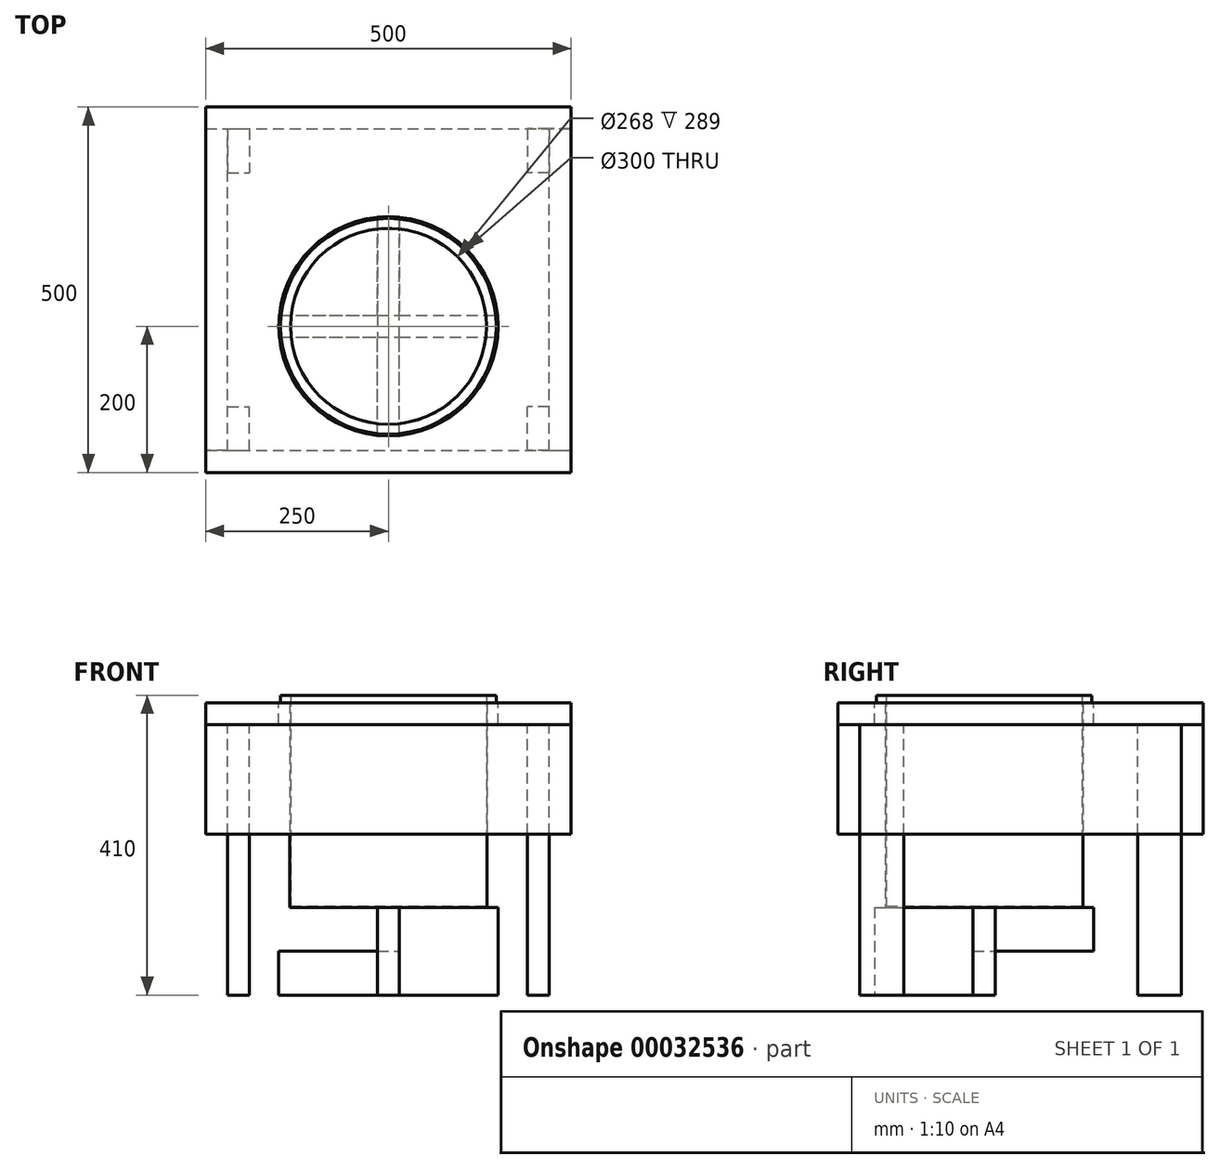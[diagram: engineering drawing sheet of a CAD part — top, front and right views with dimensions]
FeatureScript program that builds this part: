
annotation { "Feature Type Name" : "Feature", "Feature Type Description" : "" }
export const myFeature = defineFeature(function(context is Context, id is Id, definition is map)
    precondition{}
    {
        {
            var Q0;
            Q0=qCreatedBy(makeId("Top.planeOp"),FACE);
            var sketch = newSketch(context, id + "F0", { "sketchPlane" : qUnion([Q0])});
            skLineSegment(sketch, "E0.bottom", {"start": v(0, 0) * mm, "end": v(500, 0) * mm});
            skLineSegment(sketch, "E0.top", {"start": v(0, 500) * mm, "end": v(500, 500) * mm});
            skLineSegment(sketch, "E0.left", {"start": v(0, 0) * mm, "end": v(0, 500) * mm});
            skLineSegment(sketch, "E0.right", {"start": v(500, 0) * mm, "end": v(500, 500) * mm});
            skSolve(sketch);
        }
        {
            var Q0;
            Q0=makeQuery(id+"F0.imprint","IMPRINT",FACE,{"disambiguationData":[TD([[makeQuery(id+"F0.imprint","IMPRINT",EDGE,{"derivedFrom":sQuery(id+"F0.wireOp",EDGE,"E0.bottom")}),1.0]])]});
            extrude(context, id + "F1", {"entities" : qUnion([Q0]), "depth" : 30 * mm});
        }
        {
            var Q0;
            Q0=makeQuery(id+"F1.opExtrude","CAP_FACE",FACE,{"disambiguationData":[OSD([sQuery(id+"F0.wireOp",EDGE,"E0.bottom"),sQuery(id+"F0.wireOp",EDGE,"E0.top"),sQuery(id+"F0.wireOp",EDGE,"E0.left"),sQuery(id+"F0.wireOp",EDGE,"E0.right")])],"isStart":true});
            var sketch = newSketch(context, id + "F2", { "sketchPlane" : qUnion([Q0])});
            skLineSegment(sketch, "E1.bottom", {"start": v(30, -30) * mm, "end": v(60, -30) * mm});
            skLineSegment(sketch, "E1.top", {"start": v(30, -90) * mm, "end": v(60, -90) * mm});
            skLineSegment(sketch, "E1.left", {"start": v(30, -30) * mm, "end": v(30, -90) * mm});
            skLineSegment(sketch, "E1.right", {"start": v(60, -30) * mm, "end": v(60, -90) * mm});
            skLineSegment(sketch, "E2", {"start": v(30, -30) * mm, "end": v(30, 0) * mm, "construction": true});
            skLineSegment(sketch, "E3", {"start": v(30, -30) * mm, "end": v(0, -30) * mm, "construction": true});
            skLineSegment(sketch, "E4", {"start": v(250, 0) * mm, "end": v(250, -500) * mm, "construction": true});
            skLineSegment(sketch, "E5", {"start": v(0, -250) * mm, "end": v(500, -250) * mm, "construction": true});
            skLineSegment(sketch, "E6.MirrorCS", {"start": v(470, -30) * mm, "end": v(440, -30) * mm});
            skLineSegment(sketch, "E7.MirrorCS", {"start": v(470, -90) * mm, "end": v(440, -90) * mm});
            skLineSegment(sketch, "E8.MirrorCS", {"start": v(470, -30) * mm, "end": v(470, -90) * mm});
            skLineSegment(sketch, "E9.MirrorCS", {"start": v(440, -30) * mm, "end": v(440, -90) * mm});
            skLineSegment(sketch, "E10.MirrorCS", {"start": v(470, -410) * mm, "end": v(440, -410) * mm});
            skLineSegment(sketch, "E11.MirrorCS", {"start": v(440, -470) * mm, "end": v(440, -410) * mm});
            skLineSegment(sketch, "E12.MirrorCS", {"start": v(470, -470) * mm, "end": v(440, -470) * mm});
            skLineSegment(sketch, "E13.MirrorCS", {"start": v(470, -470) * mm, "end": v(470, -410) * mm});
            skLineSegment(sketch, "E14.MirrorCS", {"start": v(60, -470) * mm, "end": v(60, -410) * mm});
            skLineSegment(sketch, "E15.MirrorCS", {"start": v(30, -410) * mm, "end": v(60, -410) * mm});
            skLineSegment(sketch, "E16.MirrorCS", {"start": v(30, -470) * mm, "end": v(30, -410) * mm});
            skLineSegment(sketch, "E17.MirrorCS", {"start": v(30, -470) * mm, "end": v(60, -470) * mm});
            skSolve(sketch);
        }
        {
            var Q0;
            Q0=makeQuery(id+"F2.imprint","IMPRINT",FACE,{"disambiguationData":[TD([[makeQuery(id+"F2.imprint","IMPRINT",EDGE,{"derivedFrom":sQuery(id+"F2.wireOp",EDGE,"E1.bottom")}),-1.0]])]});
            var Q1;
            Q1=makeQuery(id+"F2.imprint","IMPRINT",FACE,{"disambiguationData":[TD([[makeQuery(id+"F2.imprint","IMPRINT",EDGE,{"derivedFrom":sQuery(id+"F2.wireOp",EDGE,"E6.MirrorCS")}),1.0]])]});
            var Q2;
            Q2=makeQuery(id+"F2.imprint","IMPRINT",FACE,{"disambiguationData":[TD([[makeQuery(id+"F2.imprint","IMPRINT",EDGE,{"derivedFrom":sQuery(id+"F2.wireOp",EDGE,"E10.MirrorCS")}),1.0]])]});
            var Q3;
            Q3=makeQuery(id+"F2.imprint","IMPRINT",FACE,{"disambiguationData":[TD([[makeQuery(id+"F2.imprint","IMPRINT",EDGE,{"derivedFrom":sQuery(id+"F2.wireOp",EDGE,"E14.MirrorCS")}),1.0]])]});
            extrude(context, id + "F19", {"entities" : qUnion([Q0, Q1, Q2, Q3]), "depth" : 370 * mm});
        }
        {
            var Q0;
            Q0=makeQuery(id+"F1.opExtrude","CAP_FACE",FACE,{"disambiguationData":[OSD([sQuery(id+"F0.wireOp",EDGE,"E0.bottom"),sQuery(id+"F0.wireOp",EDGE,"E0.top"),sQuery(id+"F0.wireOp",EDGE,"E0.left"),sQuery(id+"F0.wireOp",EDGE,"E0.right")])],"isStart":true});
            var sketch = newSketch(context, id + "F3", { "sketchPlane" : qUnion([Q0])});
            skLineSegment(sketch, "E18", {"start": v(250, 0) * mm, "end": v(250, -500) * mm, "construction": true});
            skLineSegment(sketch, "E19", {"start": v(0, -250) * mm, "end": v(500, -250) * mm, "construction": true});
            skLineSegment(sketch, "E20.MirrorCS", {"start": v(0, -470) * mm, "end": v(30, -470) * mm});
            skLineSegment(sketch, "E21.MirrorCS", {"start": v(500, -470) * mm, "end": v(470, -470) * mm});
            skLineSegment(sketch, "E22", {"start": v(30, -30) * mm, "end": v(30, -470) * mm});
            skLineSegment(sketch, "E23", {"start": v(30, -30) * mm, "end": v(470, -30) * mm});
            skLineSegment(sketch, "E24.MirrorCS", {"start": v(30, -470) * mm, "end": v(470, -470) * mm});
            skLineSegment(sketch, "E25.MirrorCS", {"start": v(470, -30) * mm, "end": v(470, -470) * mm});
            skLineSegment(sketch, "E26", {"start": v(470, -30) * mm, "end": v(500, -30) * mm});
            skLineSegment(sketch, "E27", {"start": v(30, -30) * mm, "end": v(0, -30) * mm});
            skSolve(sketch);
        }
        {
            var Q0;
            Q0=makeQuery(id+"F3.imprint","IMPRINT",FACE,{"disambiguationData":[TD([[makeQuery(id+"F3.imprint","IMPRINT",EDGE,{"derivedFrom":sQuery(id+"F3.wireOp",EDGE,"E23")}),1.0]])]});
            extrude(context, id + "F20", {"entities" : qUnion([Q0]), "depth" : 150 * mm});
        }
        {
            var Q0;
            {var subQ0=sQuery(id+"F3.wireOp",EDGE,"E20.MirrorCS");Q0=makeQuery(id+"F3.imprint","IMPRINT",FACE,{"disambiguationData":[TD([[makeQuery(id+"F3.imprint","IMPRINT",EDGE,{"derivedFrom":subQ0}),1.0]])]});}
            var Q1;
            {var subQ0=sQuery(id+"F3.wireOp",EDGE,"E21.MirrorCS");Q1=makeQuery(id+"F3.imprint","IMPRINT",FACE,{"disambiguationData":[TD([[makeQuery(id+"F3.imprint","IMPRINT",EDGE,{"derivedFrom":subQ0}),-1.0]])]});}
            extrude(context, id + "F4", {"entities" : qUnion([Q0, Q1]), "depth" : 150 * mm});
        }
        {
            var Q0;
            Q0=makeQuery(id+"F3.imprint","IMPRINT",FACE,{"disambiguationData":[TD([[makeQuery(id+"F3.imprint","IMPRINT",EDGE,{"derivedFrom":sQuery(id+"F3.wireOp",EDGE,"E20.MirrorCS")}),-1.0]])]});
            extrude(context, id + "F5", {"entities" : qUnion([Q0]), "depth" : 150 * mm});
        }
        {
            var Q0;
            Q0=makeQuery(id+"F1.opExtrude","CAP_FACE",FACE,{"disambiguationData":[OSD([sQuery(id+"F0.wireOp",EDGE,"E0.bottom"),sQuery(id+"F0.wireOp",EDGE,"E0.top"),sQuery(id+"F0.wireOp",EDGE,"E0.left"),sQuery(id+"F0.wireOp",EDGE,"E0.right")])],"isStart":false});
            var sketch = newSketch(context, id + "F6", { "sketchPlane" : qUnion([Q0])});
            skLineSegment(sketch, "E28", {"start": v(0, 200) * mm, "end": v(500, 200) * mm, "construction": true});
            skCircle(sketch, "E29", {"center": v(250, 200) * mm, "radius": 150 * mm});
            skSolve(sketch);
        }
        {
            var Q0;
            Q0=makeQuery(id+"F6.imprint","IMPRINT",FACE,{"disambiguationData":[TD([[makeQuery(id+"F6.imprint","IMPRINT",EDGE,{"derivedFrom":sQuery(id+"F6.wireOp",EDGE,"E29")}),1.0]])]});
            extrude(context, id + "F21", {"entities" : qUnion([Q0]), "operationType" : NewBodyOperationType.REMOVE, "endBound" : BoundingType.THROUGH_ALL, "oppositeDirection" : true, "depth" : 25 * mm});
        }
        {
            var Q0;
            Q0=makeQuery(id+"F19.opExtrude","CAP_FACE",FACE,{"disambiguationData":[OSD([sQuery(id+"F2.wireOp",EDGE,"E6.MirrorCS"),sQuery(id+"F2.wireOp",EDGE,"E7.MirrorCS"),sQuery(id+"F2.wireOp",EDGE,"E8.MirrorCS"),sQuery(id+"F2.wireOp",EDGE,"E9.MirrorCS")])],"isStart":false});
            var sketch = newSketch(context, id + "F7", { "sketchPlane" : qUnion([Q0])});
            skCircle(sketch, "E30.0", {"center": v(250, -200) * mm, "radius": 150 * mm, "construction": true});
            skLineSegment(sketch, "E31.bottom", {"start": v(400, -350) * mm, "end": v(100, -350) * mm});
            skLineSegment(sketch, "E31.top", {"start": v(400, -50) * mm, "end": v(100, -50) * mm});
            skLineSegment(sketch, "E31.left", {"start": v(400, -350) * mm, "end": v(400, -50) * mm});
            skLineSegment(sketch, "E31.right", {"start": v(100, -350) * mm, "end": v(100, -50) * mm});
            skLineSegment(sketch, "E32", {"start": v(235, -50) * mm, "end": v(235, -350) * mm});
            skLineSegment(sketch, "E33", {"start": v(265, -50) * mm, "end": v(265, -350) * mm});
            skLineSegment(sketch, "E34", {"start": v(235, -200) * mm, "end": v(250, -200) * mm, "construction": true});
            skLineSegment(sketch, "E35", {"start": v(250, -200) * mm, "end": v(265, -200) * mm, "construction": true});
            skLineSegment(sketch, "E36", {"start": v(100, -185) * mm, "end": v(400, -185) * mm});
            skLineSegment(sketch, "E37", {"start": v(100, -215) * mm, "end": v(400, -215) * mm});
            skLineSegment(sketch, "E38", {"start": v(250, -185) * mm, "end": v(250, -200) * mm});
            skLineSegment(sketch, "E39", {"start": v(250, -200) * mm, "end": v(250, -215) * mm});
            skSolve(sketch);
        }
        {
            var Q0;
            {var subQ2=sQuery(id+"F7.wireOp",EDGE,"E32");var subQ5=sQuery(id+"F7.wireOp",EDGE,"E31.top");var subQ8=makeQuery(id+"F7.imprint","INTERSECT",VERTEX,{"derivedFrom":[subQ5,subQ2]});Q0=makeQuery(id+"F7.imprint","IMPRINT",FACE,{"disambiguationData":[TD([[makeQuery(id+"F7.imprint","IMPRINT",EDGE,{"disambiguationData":[TD([[subQ8,1.0]])],"derivedFrom":subQ5}),1.0]])]});}
            var Q1;
            {var subQ4=sQuery(id+"F7.wireOp",EDGE,"E38");Q1=makeQuery(id+"F7.imprint","IMPRINT",FACE,{"disambiguationData":[TD([[makeQuery(id+"F7.imprint","IMPRINT",EDGE,{"derivedFrom":subQ4}),-1.0]])]});}
            var Q2;
            {var subQ0=sQuery(id+"F7.wireOp",EDGE,"E38");Q2=makeQuery(id+"F7.imprint","IMPRINT",FACE,{"disambiguationData":[TD([[makeQuery(id+"F7.imprint","IMPRINT",EDGE,{"derivedFrom":subQ0}),1.0]])]});}
            var Q3;
            {var subQ1=sQuery(id+"F7.wireOp",EDGE,"E31.bottom");var subQ5=sQuery(id+"F7.wireOp",EDGE,"E32");var subQ6=makeQuery(id+"F7.imprint","INTERSECT",VERTEX,{"derivedFrom":[subQ1,subQ5]});Q3=makeQuery(id+"F7.imprint","IMPRINT",FACE,{"disambiguationData":[TD([[makeQuery(id+"F7.imprint","IMPRINT",EDGE,{"disambiguationData":[TD([[subQ6,1.0]])],"derivedFrom":subQ1}),-1.0]])]});}
            extrude(context, id + "F8", {"entities" : qUnion([Q0, Q1, Q2, Q3]), "oppositeDirection" : true, "depth" : 120 * mm});
        }
        {
            var Q0;
            {var subQ0=sQuery(id+"F7.wireOp",EDGE,"E36");var subQ1=sQuery(id+"F7.wireOp",EDGE,"E31.right");var subQ2=makeQuery(id+"F7.imprint","INTERSECT",VERTEX,{"derivedFrom":[subQ1,subQ0]});Q0=makeQuery(id+"F7.imprint","IMPRINT",FACE,{"disambiguationData":[TD([[makeQuery(id+"F7.imprint","IMPRINT",EDGE,{"disambiguationData":[TD([[subQ2,1.0]])],"derivedFrom":subQ1}),-1.0]])]});}
            var Q1;
            {var subQ0=sQuery(id+"F7.wireOp",EDGE,"E38");Q1=makeQuery(id+"F7.imprint","IMPRINT",FACE,{"disambiguationData":[TD([[makeQuery(id+"F7.imprint","IMPRINT",EDGE,{"derivedFrom":subQ0}),1.0]])]});}
            var Q2;
            {var subQ4=sQuery(id+"F7.wireOp",EDGE,"E38");Q2=makeQuery(id+"F7.imprint","IMPRINT",FACE,{"disambiguationData":[TD([[makeQuery(id+"F7.imprint","IMPRINT",EDGE,{"derivedFrom":subQ4}),-1.0]])]});}
            var Q3;
            {var subQ0=sQuery(id+"F7.wireOp",EDGE,"E36");var subQ1=sQuery(id+"F7.wireOp",EDGE,"E31.left");var subQ2=makeQuery(id+"F7.imprint","INTERSECT",VERTEX,{"derivedFrom":[subQ1,subQ0]});Q3=makeQuery(id+"F7.imprint","IMPRINT",FACE,{"disambiguationData":[TD([[makeQuery(id+"F7.imprint","IMPRINT",EDGE,{"disambiguationData":[TD([[subQ2,1.0]])],"derivedFrom":subQ1}),1.0]])]});}
            extrude(context, id + "F9", {"entities" : qUnion([Q0, Q1, Q2, Q3]), "oppositeDirection" : true, "depth" : 120 * mm});
        }
        {
            var Q0;
            Q0=makeQuery(id+"F8.opExtrude","SWEPT_FACE",FACE,{"disambiguationData":[OSD([sQuery(id+"F7.wireOp",EDGE,"E33")])]});
            var sketch = newSketch(context, id + "F10", { "sketchPlane" : qUnion([Q0])});
            skLineSegment(sketch, "E40.0.0", {"start": v(185, -370) * mm, "end": v(215, -370) * mm, "construction": true});
            skLineSegment(sketch, "E40.0.1", {"start": v(215, -370) * mm, "end": v(215, -310) * mm, "construction": true});
            skLineSegment(sketch, "E40.0.2", {"start": v(215, -250) * mm, "end": v(185, -250) * mm});
            skLineSegment(sketch, "E40.0.3", {"start": v(185, -250) * mm, "end": v(185, -310) * mm});
            skLineSegment(sketch, "E41", {"start": v(185, -310) * mm, "end": v(185, -370) * mm, "construction": true});
            skLineSegment(sketch, "E42", {"start": v(215, -310) * mm, "end": v(215, -250) * mm});
            skLineSegment(sketch, "E43", {"start": v(185, -310) * mm, "end": v(215, -310) * mm});
            skSolve(sketch);
        }
        {
            var Q0;
            Q0=makeQuery(id+"F10.imprint","IMPRINT",FACE,{"disambiguationData":[TD([[makeQuery(id+"F10.imprint","IMPRINT",EDGE,{"derivedFrom":sQuery(id+"F10.wireOp",EDGE,"E40.0.2")}),-1.0]])]});
            extrude(context, id + "F11", {"entities" : qUnion([Q0]), "operationType" : NewBodyOperationType.REMOVE, "endBound" : BoundingType.THROUGH_ALL, "oppositeDirection" : true, "depth" : 25 * mm});
        }
        {
            var Q0;
            Q0=makeQuery(id+"F9.opExtrude","SWEPT_FACE",FACE,{"disambiguationData":[OSD([sQuery(id+"F7.wireOp",EDGE,"E36")])]});
            var sketch = newSketch(context, id + "F12", { "sketchPlane" : qUnion([Q0])});
            skLineSegment(sketch, "E44.0.0", {"start": v(235, -370) * mm, "end": v(265, -370) * mm});
            skLineSegment(sketch, "E44.0.1", {"start": v(265, -370) * mm, "end": v(265, -310) * mm});
            skLineSegment(sketch, "E44.0.2", {"start": v(265, -250) * mm, "end": v(235, -250) * mm, "construction": true});
            skLineSegment(sketch, "E44.0.3", {"start": v(235, -250) * mm, "end": v(235, -310) * mm, "construction": true});
            skLineSegment(sketch, "E45", {"start": v(235, -310) * mm, "end": v(235, -370) * mm});
            skLineSegment(sketch, "E46", {"start": v(265, -310) * mm, "end": v(265, -250) * mm, "construction": true});
            skLineSegment(sketch, "E47", {"start": v(235, -310) * mm, "end": v(265, -310) * mm});
            skSolve(sketch);
        }
        {
            var Q0;
            Q0=makeQuery(id+"F12.imprint","IMPRINT",FACE,{"disambiguationData":[TD([[makeQuery(id+"F12.imprint","IMPRINT",EDGE,{"derivedFrom":sQuery(id+"F12.wireOp",EDGE,"E44.0.0")}),1.0]])]});
            extrude(context, id + "F13", {"entities" : qUnion([Q0]), "operationType" : NewBodyOperationType.REMOVE, "endBound" : BoundingType.THROUGH_ALL, "oppositeDirection" : true, "depth" : 25 * mm});
        }
        {
            var Q0;
            Q0=makeQuery(id+"F9.opExtrude","CAP_FACE",FACE,{"disambiguationData":[OSD([sQuery(id+"F7.wireOp",EDGE,"E31.left"),sQuery(id+"F7.wireOp",EDGE,"E31.right"),sQuery(id+"F7.wireOp",EDGE,"E36"),sQuery(id+"F7.wireOp",EDGE,"E37")])],"isStart":false});
            var sketch = newSketch(context, id + "F14", { "sketchPlane" : qUnion([Q0])});
            skCircle(sketch, "E48.0", {"center": v(250, 200) * mm, "radius": 150 * mm, "construction": true});
            skCircle(sketch, "E49", {"center": v(250, 200) * mm, "radius": 135 * mm});
            skSolve(sketch);
        }
        {
            var Q0;
            {var subQ0=sQuery(id+"F14.wireOp",EDGE,"E49");var subQ1=makeQuery(id+"F9.opExtrude","CAP_EDGE",EDGE,{"disambiguationData":[OSD([sQuery(id+"F7.wireOp",EDGE,"E37")])],"isStart":false});var subQ2=makeQuery(id+"F14.imprint","INTERSECT",VERTEX,{"disambiguationData":[OD(0.0)],"derivedFrom":[subQ1,subQ0]});Q0=makeQuery(id+"F14.imprint","IMPRINT",FACE,{"disambiguationData":[TD([[makeQuery(id+"F14.imprint","IMPRINT",EDGE,{"disambiguationData":[TD([[subQ2,1.0]])],"derivedFrom":subQ0}),1.0]])]});}
            var Q1;
            {var subQ0=sQuery(id+"F14.wireOp",EDGE,"E49");var subQ1=makeQuery(id+"F9.opExtrude","CAP_EDGE",EDGE,{"disambiguationData":[OSD([sQuery(id+"F7.wireOp",EDGE,"E36")])],"isStart":false});var subQ2=makeQuery(id+"F14.imprint","INTERSECT",VERTEX,{"disambiguationData":[OD(0.0)],"derivedFrom":[subQ1,subQ0]});Q1=makeQuery(id+"F14.imprint","IMPRINT",FACE,{"disambiguationData":[TD([[makeQuery(id+"F14.imprint","IMPRINT",EDGE,{"disambiguationData":[TD([[subQ2,-1.0]])],"derivedFrom":subQ0}),1.0]])]});}
            var Q2;
            {var subQ0=sQuery(id+"F14.wireOp",EDGE,"E49");var subQ1=makeQuery(id+"F9.opExtrude","CAP_EDGE",EDGE,{"disambiguationData":[OSD([sQuery(id+"F7.wireOp",EDGE,"E37")])],"isStart":false});var subQ2=makeQuery(id+"F14.imprint","INTERSECT",VERTEX,{"disambiguationData":[OD(0.0)],"derivedFrom":[subQ1,subQ0]});Q2=makeQuery(id+"F14.imprint","IMPRINT",FACE,{"disambiguationData":[TD([[makeQuery(id+"F14.imprint","IMPRINT",EDGE,{"disambiguationData":[TD([[subQ2,-1.0]])],"derivedFrom":subQ0}),1.0]])]});}
            extrude(context, id + "F15", {"entities" : qUnion([Q0, Q1, Q2]), "depth" : 280 * mm});
        }
        {
            var Q0;
            Q0=makeQuery(id+"F15.opExtrude","CAP_FACE",FACE,{"disambiguationData":[OSD([sQuery(id+"F14.wireOp",EDGE,"E49")])],"isStart":false});
            shell(context, id + "F16", {"entities" : qUnion([Q0]), "thickness" : 1 * mm});
        }
        {
            var Q0;
            Q0=makeQuery(id+"F15.opExtrude","CAP_FACE",FACE,{"disambiguationData":[OSD([sQuery(id+"F14.wireOp",EDGE,"E49")])],"isStart":false});
            var sketch = newSketch(context, id + "F17", { "sketchPlane" : qUnion([Q0])});
            skCircle(sketch, "E50.0", {"center": v(250, 200) * mm, "radius": 134 * mm, "construction": true});
            skCircle(sketch, "E51", {"center": v(250, 200) * mm, "radius": 147.5 * mm});
            skSolve(sketch);
        }
        {
            var Q0;
            Q0=makeQuery(id+"F17.imprint","IMPRINT",FACE,{"disambiguationData":[TD([[makeQuery(id+"F17.imprint","IMPRINT",EDGE,{"derivedFrom":sQuery(id+"F17.wireOp",EDGE,"E51")}),1.0]])]});
            var Q1;
            {var subQ0=sQuery(id+"F14.wireOp",EDGE,"E49");var subQ1=makeQuery(id+"F15.opExtrude","CAP_EDGE",EDGE,{"disambiguationData":[OSD([subQ0])],"isStart":false});Q1=makeQuery(id+"F17.imprint","IMPRINT",FACE,{"disambiguationData":[TD([[makeQuery(id+"F17.imprint","IMPRINT",EDGE,{"derivedFrom":subQ1}),1.0]])]});}
            extrude(context, id + "F18", {"entities" : qUnion([Q0, Q1]), "operationType" : NewBodyOperationType.ADD, "depth" : 10 * mm});
        }
    });
